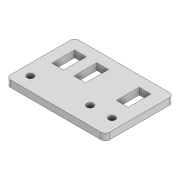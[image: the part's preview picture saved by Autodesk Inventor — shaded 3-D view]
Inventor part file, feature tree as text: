
AUTODESK INVENTOR PART (.ipt)
format: ipt  version: 2022 (Build 260153000, 153)  size: 149,504 bytes
history: native  units: mm
features: thicken_offset x3, extrude x1, fillet x1
ambient origin geometry x8: Origin, YZ Plane, XZ Plane, XY Plane, X Axis, Y Axis, Z Axis, Center Point
bodies: Solid1 (feature_tree)
feature tree (5):
  extrude  "Extrusion1"  Depth=3.0mm
  fillet  "Fillet1"  Radius=3.0mm
  thicken_offset  "Thicken1"
  thicken_offset  "Thicken2"
  thicken_offset  "Thicken3"
